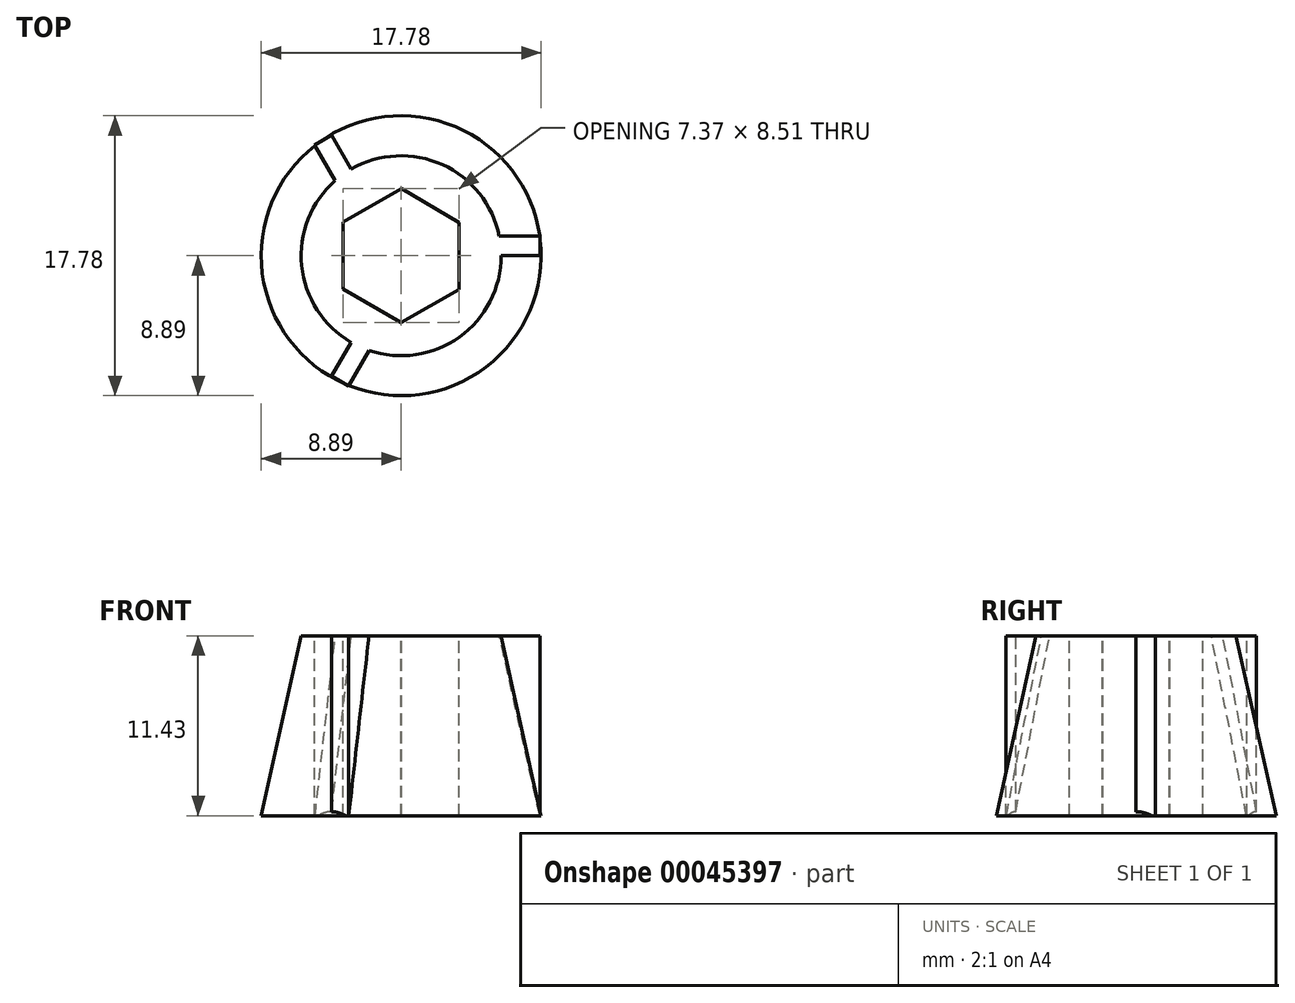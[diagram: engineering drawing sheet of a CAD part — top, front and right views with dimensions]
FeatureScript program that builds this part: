
annotation { "Feature Type Name" : "Feature", "Feature Type Description" : "" }
export const myFeature = defineFeature(function(context is Context, id is Id, definition is map)
    precondition{}
    {
        {
            var Q0;
            Q0=qCreatedBy(makeId("Front.planeOp"),FACE);
            var sketch = newSketch(context, id + "F0", { "sketchPlane" : qUnion([Q0])});
            skLineSegment(sketch, "E0", {"start": v(0, 0) * mm, "end": v(0, 11.43) * mm});
            skLineSegment(sketch, "E1", {"start": v(0, 11.43) * mm, "end": v(-6.35, 11.43) * mm});
            skLineSegment(sketch, "E2", {"start": v(-6.35, 11.43) * mm, "end": v(-8.9, 0) * mm});
            skLineSegment(sketch, "E3", {"start": v(-8.9, 0) * mm, "end": v(0, 0) * mm});
            skLineSegment(sketch, "E4", {"start": v(0, 0) * mm, "end": v(0, -33.43) * mm, "construction": true});
            skSolve(sketch);
        }
        {
            var Q0;
            Q0=makeQuery(id+"F0.imprint","IMPRINT",FACE,{"disambiguationData":[TD([[makeQuery(id+"F0.imprint","IMPRINT",EDGE,{"derivedFrom":sQuery(id+"F0.wireOp",EDGE,"E0")}),1.0]])]});
            var Q1;
            Q1=sQuery(id+"F0.wireOp",EDGE,"E0");
            revolve(context, id + "F1", {"entities" : qUnion([Q0]), "axis" : qUnion([Q1]), "revolveType" : RevolveType.FULL});
        }
        {
            var Q0;
            Q0=makeQuery(id+"F1.opRevolve","SWEPT_FACE",FACE,{"disambiguationData":[OSD([sQuery(id+"F0.wireOp",EDGE,"E1")])]});
            var sketch = newSketch(context, id + "F2", { "sketchPlane" : qUnion([Q0])});
            skCircle(sketch, "E5.cCircle", {"center": v(0, 0) * mm, "radius": 3.68 * mm, "construction": true});
            skLineSegment(sketch, "E5.0", {"start": v(0, 4.25) * mm, "end": v(3.69, 2.12) * mm});
            skLineSegment(sketch, "E5.1", {"start": v(3.69, 2.12) * mm, "end": v(3.68, -2.13) * mm});
            skLineSegment(sketch, "E5.2", {"start": v(3.68, -2.13) * mm, "end": v(0, -4.25) * mm});
            skLineSegment(sketch, "E5.3", {"start": v(0, -4.25) * mm, "end": v(-3.69, -2.12) * mm});
            skLineSegment(sketch, "E5.4", {"start": v(-3.69, -2.12) * mm, "end": v(-3.68, 2.13) * mm});
            skLineSegment(sketch, "E5.5", {"start": v(-3.68, 2.13) * mm, "end": v(0, 4.25) * mm});
            skPoint(sketch, "E5.0.midPoint", {"position": v(1.85, 3.19) * mm});
            skLineSegment(sketch, "E6", {"start": v(-3.69, -2.12) * mm, "end": v(3.68, -2.13) * mm, "construction": true});
            skSolve(sketch);
        }
        {
            var Q0;
            Q0=makeQuery(id+"F2.imprint","IMPRINT",FACE,{"disambiguationData":[TD([[makeQuery(id+"F2.imprint","IMPRINT",EDGE,{"derivedFrom":sQuery(id+"F2.wireOp",EDGE,"E5.0")}),-1.0]])]});
            extrude(context, id + "F3", {"entities" : qUnion([Q0]), "operationType" : NewBodyOperationType.REMOVE, "oppositeDirection" : true, "depth" : 25.4 * mm});
        }
        {
            var Q0;
            Q0=makeQuery(id+"F1.opRevolve","SWEPT_FACE",FACE,{"disambiguationData":[OSD([sQuery(id+"F0.wireOp",EDGE,"E1")])]});
            var sketch = newSketch(context, id + "F4", { "sketchPlane" : qUnion([Q0])});
            skLineSegment(sketch, "E7.bottom", {"start": v(6.23, 1.24) * mm, "end": v(8.83, 1.24) * mm});
            skLineSegment(sketch, "E7.top", {"start": v(6.23, 0) * mm, "end": v(8.83, 0) * mm});
            skLineSegment(sketch, "E7.left", {"start": v(6.23, 1.24) * mm, "end": v(6.23, 0) * mm});
            skLineSegment(sketch, "E7.right", {"start": v(8.83, 1.24) * mm, "end": v(8.83, 0) * mm});
            skLineSegment(sketch, "E8.1.0", {"start": v(-4.19, 4.78) * mm, "end": v(-5.49, 7.03) * mm});
            skLineSegment(sketch, "E8.1.1", {"start": v(-5.49, 7.03) * mm, "end": v(-4.42, 7.65) * mm});
            skLineSegment(sketch, "E8.1.2", {"start": v(-3.11, 5.4) * mm, "end": v(-4.42, 7.65) * mm});
            skLineSegment(sketch, "E8.1.3", {"start": v(-4.19, 4.78) * mm, "end": v(-3.11, 5.4) * mm});
            skLineSegment(sketch, "E8.2.0", {"start": v(-2.04, -6.01) * mm, "end": v(-3.35, -8.27) * mm});
            skLineSegment(sketch, "E8.2.1", {"start": v(-3.35, -8.27) * mm, "end": v(-4.42, -7.65) * mm});
            skLineSegment(sketch, "E8.2.2", {"start": v(-3.11, -5.4) * mm, "end": v(-4.42, -7.65) * mm});
            skLineSegment(sketch, "E8.2.3", {"start": v(-2.04, -6.01) * mm, "end": v(-3.11, -5.4) * mm});
            skPoint(sketch, "E8.center", {"position": v(0, 0) * mm});
            skSolve(sketch);
        }
        {
            var Q0;
            {var subQ3=sQuery(id+"F4.wireOp",EDGE,"E7.bottom");Q0=makeQuery(id+"F4.imprint","IMPRINT",FACE,{"disambiguationData":[TD([[makeQuery(id+"F4.imprint","IMPRINT",EDGE,{"derivedFrom":subQ3}),-1.0]])]});}
            var Q1;
            {var subQ4=sQuery(id+"F4.wireOp",EDGE,"E8.1.0");Q1=makeQuery(id+"F4.imprint","IMPRINT",FACE,{"disambiguationData":[TD([[makeQuery(id+"F4.imprint","IMPRINT",EDGE,{"derivedFrom":subQ4}),-1.0]])]});}
            var Q2;
            {var subQ3=sQuery(id+"F4.wireOp",EDGE,"E8.2.0");Q2=makeQuery(id+"F4.imprint","IMPRINT",FACE,{"disambiguationData":[TD([[makeQuery(id+"F4.imprint","IMPRINT",EDGE,{"derivedFrom":subQ3}),-1.0]])]});}
            extrude(context, id + "F5", {"entities" : qUnion([Q0, Q1, Q2]), "operationType" : NewBodyOperationType.ADD, "oppositeDirection" : true, "depth" : 11.43 * mm});
        }
    });
